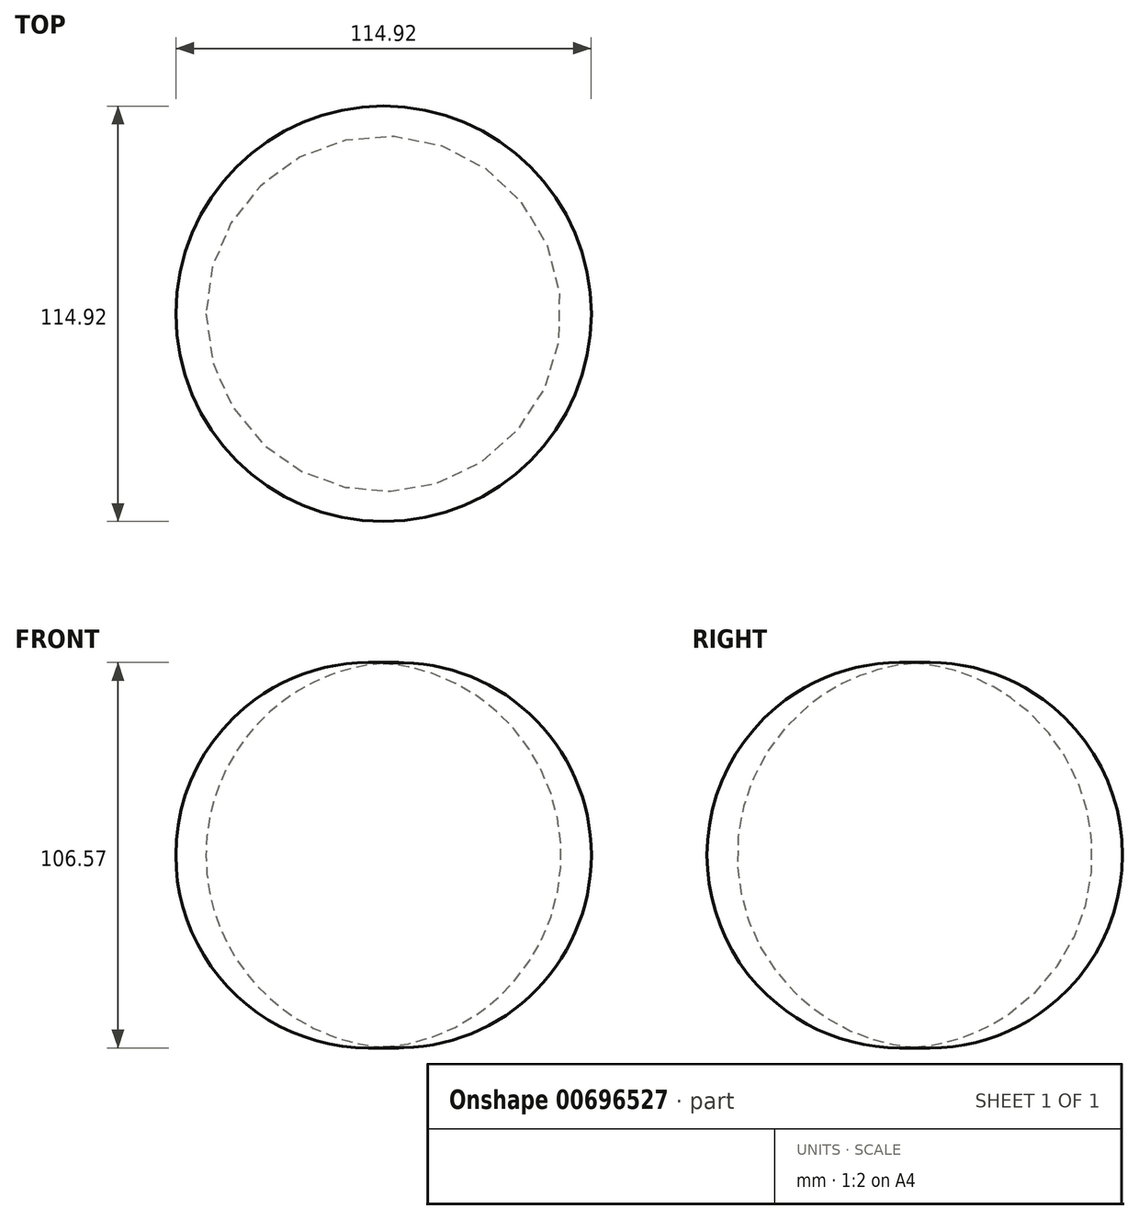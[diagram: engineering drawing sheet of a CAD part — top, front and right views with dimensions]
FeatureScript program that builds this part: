
annotation { "Feature Type Name" : "Feature", "Feature Type Description" : "" }
export const myFeature = defineFeature(function(context is Context, id is Id, definition is map)
    precondition{}
    {
        {
            var Q0;
            Q0=qCreatedBy(makeId("Front.planeOp"),FACE);
            var sketch = newSketch(context, id + "F0", { "sketchPlane" : qUnion([Q0])});
            skLineSegment(sketch, "E0", {"start": v(0, 52.99) * mm, "end": v(0, -53.26) * mm});
            skArc(sketch, "E1", {"start": v(0, 52.99) * mm, "mid": v(-49.11, -0.13) * mm, "end": v(0, -53.26) * mm});
            skSolve(sketch);
        }
        {
            var Q0;
            Q0=makeQuery(id+"F0.imprint","IMPRINT",FACE,{"disambiguationData":[TD([[makeQuery(id+"F0.imprint","IMPRINT",EDGE,{"derivedFrom":sQuery(id+"F0.wireOp",EDGE,"E0")}),-1.0]])]});
            var Q1;
            Q1=sQuery(id+"F0.wireOp",EDGE,"E0");
            revolve(context, id + "F1", {"entities" : qUnion([Q0]), "axis" : qUnion([Q1]), "revolveType" : RevolveType.FULL});
        }
        {
            var Q0;
            Q0=qCreatedBy(makeId("Top.planeOp"),FACE);
            var sketch = newSketch(context, id + "F2", { "sketchPlane" : qUnion([Q0])});
            skCircle(sketch, "E2", {"center": v(0, 0) * mm, "radius": 20.58 * mm});
            skSolve(sketch);
        }
        {
            var Q0;
            Q0 = qSketchRegion(id + "F2", true);
            extrude(context, id + "F3", {"entities" : qUnion([Q0]), "operationType" : NewBodyOperationType.ADD, "depth" : 25.4 * mm, "offsetDistance" : 25.4 * mm, "hasDraft" : true, "draftAngle" : 3 * degree, "hasSecondDirection" : true, "secondDirectionOppositeDirection" : true, "secondDirectionDepth" : 25.4 * mm});
        }
    });
